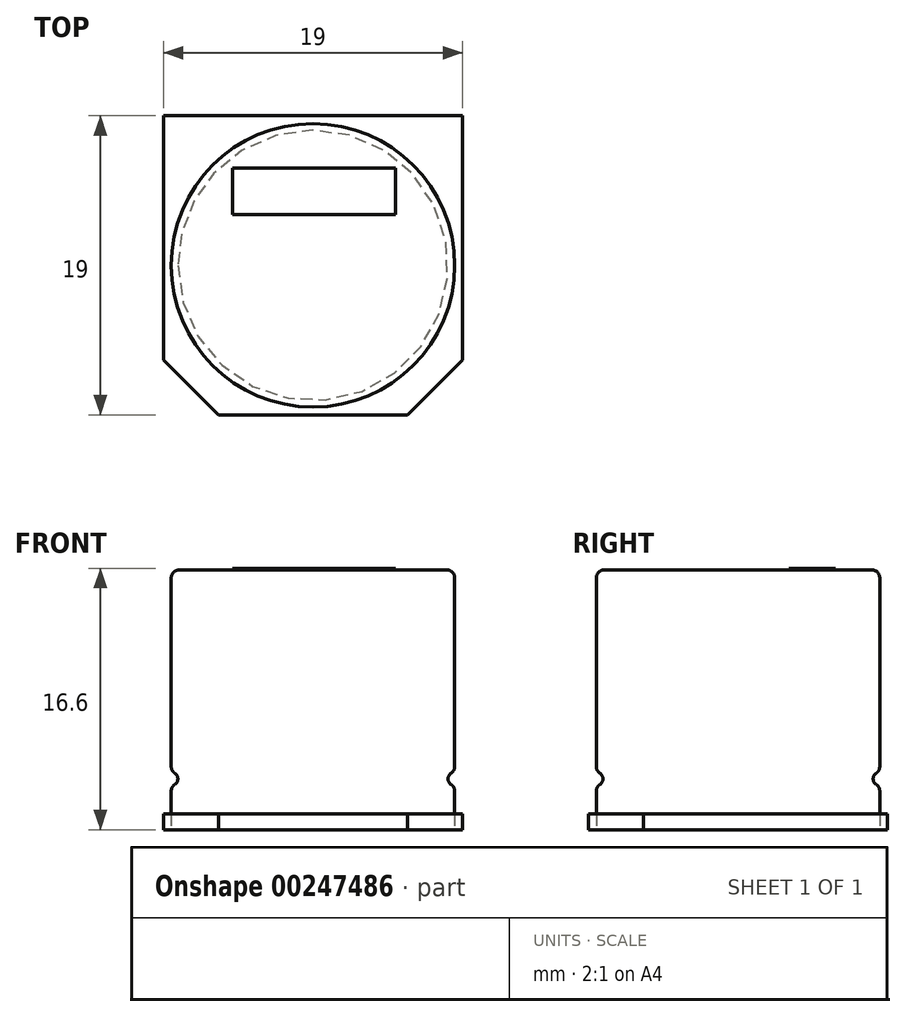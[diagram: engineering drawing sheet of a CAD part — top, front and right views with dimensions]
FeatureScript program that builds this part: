
annotation { "Feature Type Name" : "Feature", "Feature Type Description" : "" }
export const myFeature = defineFeature(function(context is Context, id is Id, definition is map)
    precondition{}
    {
        {
            var Q0;
            Q0=qCreatedBy(makeId("Front.planeOp"),FACE);
            var sketch = newSketch(context, id + "F0", { "sketchPlane" : qUnion([Q0])});
            skLineSegment(sketch, "E0.bottom", {"start": v(0, 0) * mm, "end": v(9, 0) * mm});
            skLineSegment(sketch, "E0.top", {"start": v(0, 16.5) * mm, "end": v(9, 16.5) * mm});
            skLineSegment(sketch, "E0.left", {"start": v(0, 0) * mm, "end": v(0, 16.5) * mm});
            skLineSegment(sketch, "E0.right", {"start": v(9, 0) * mm, "end": v(9, 2.8) * mm});
            skArc(sketch, "E1", {"start": v(9, 3.66) * mm, "mid": v(8.58, 3.23) * mm, "end": v(9, 2.8) * mm});
            skLineSegment(sketch, "E2.trimOffspring", {"start": v(9, 3.66) * mm, "end": v(9, 16.5) * mm});
            skSolve(sketch);
        }
        {
            var Q0;
            Q0=makeQuery(id+"F0.imprint","IMPRINT",FACE,{"disambiguationData":[TD([[makeQuery(id+"F0.imprint","IMPRINT",EDGE,{"derivedFrom":sQuery(id+"F0.wireOp",EDGE,"E0.bottom")}),1.0]])]});
            var Q1;
            Q1=sQuery(id+"F0.wireOp",EDGE,"E0.left");
            revolve(context, id + "F1", {"entities" : qUnion([Q0]), "axis" : qUnion([Q1]), "revolveType" : RevolveType.FULL});
        }
        {
            var Q0;
            Q0=makeQuery(id+"F1.opRevolve","SWEPT_EDGE",EDGE,{"disambiguationData":[OSD([sQuery(id+"F0.wireOp",EDGE,"E0.top"),sQuery(id+"F0.wireOp",EDGE,"E2.trimOffspring")])]});
            var Q1;
            Q1=makeQuery(id+"F1.opRevolve","SWEPT_EDGE",EDGE,{"disambiguationData":[OSD([sQuery(id+"F0.wireOp",EDGE,"E1"),sQuery(id+"F0.wireOp",EDGE,"E2.trimOffspring")])]});
            var Q2;
            Q2=makeQuery(id+"F1.opRevolve","SWEPT_EDGE",EDGE,{"disambiguationData":[OSD([sQuery(id+"F0.wireOp",EDGE,"E0.right"),sQuery(id+"F0.wireOp",EDGE,"E1")])]});
            fillet(context, id + "F2", {"entities" : qUnion([Q0, Q1, Q2]), "radius" : .5 * mm, "tangentPropagation" : true, "allowEdgeOverflow" : false});
        }
        {
            var Q0;
            Q0=makeQuery(id+"F1.opRevolve","SWEPT_FACE",FACE,{"disambiguationData":[OSD([sQuery(id+"F0.wireOp",EDGE,"E0.bottom")])]});
            var sketch = newSketch(context, id + "F3", { "sketchPlane" : qUnion([Q0])});
            skLineSegment(sketch, "E3.rect.bottom", {"start": v(9.5, -9.5) * mm, "end": v(-9.5, -9.5) * mm});
            skLineSegment(sketch, "E3.rect.top", {"start": v(9.5, 9.5) * mm, "end": v(-9.5, 9.5) * mm});
            skLineSegment(sketch, "E3.rect.left", {"start": v(9.5, -9.5) * mm, "end": v(9.5, 9.5) * mm});
            skLineSegment(sketch, "E3.rect.right", {"start": v(-9.5, -9.5) * mm, "end": v(-9.5, 9.5) * mm});
            skPoint(sketch, "E3.rect.middle", {"position": v(0, 0) * mm});
            skSolve(sketch);
        }
        {
            var Q0;
            Q0=qSketchRegion(id+"F3",true);
            extrude(context, id + "F4", {"entities" : qUnion([Q0]), "oppositeDirection" : true, "depth" : 1 * mm});
        }
        {
            var Q0;
            Q0=makeQuery(id+"F4.opExtrude","SWEPT_EDGE",EDGE,{"disambiguationData":[OSD([sQuery(id+"F3.wireOp",EDGE,"E3.rect.top"),sQuery(id+"F3.wireOp",EDGE,"E3.rect.right")])]});
            var Q1;
            Q1=makeQuery(id+"F4.opExtrude","SWEPT_EDGE",EDGE,{"disambiguationData":[OSD([sQuery(id+"F3.wireOp",EDGE,"E3.rect.top"),sQuery(id+"F3.wireOp",EDGE,"E3.rect.left")])]});
            chamfer(context, id + "F5", {"entities" : qUnion([Q0, Q1]), "width" : 3.5 * mm, "tangentPropagation" : true});
        }
        {
            var Q0;
            Q0=makeQuery(id+"F1.opRevolve","SWEPT_FACE",FACE,{"disambiguationData":[OSD([sQuery(id+"F0.wireOp",EDGE,"E0.top")])]});
            var sketch = newSketch(context, id + "F6", { "sketchPlane" : qUnion([Q0])});
            skLineSegment(sketch, "E4.bottom", {"start": v(-5.12, 6.19) * mm, "end": v(5.24, 6.19) * mm});
            skLineSegment(sketch, "E4.top", {"start": v(-5.12, 3.24) * mm, "end": v(5.24, 3.24) * mm});
            skLineSegment(sketch, "E4.left", {"start": v(-5.12, 6.19) * mm, "end": v(-5.12, 3.24) * mm});
            skLineSegment(sketch, "E4.right", {"start": v(5.24, 6.19) * mm, "end": v(5.24, 3.24) * mm});
            skSolve(sketch);
        }
        {
            var Q0;
            Q0=makeQuery(id+"F6.imprint","IMPRINT",FACE,{"disambiguationData":[TD([[makeQuery(id+"F6.imprint","IMPRINT",EDGE,{"derivedFrom":sQuery(id+"F6.wireOp",EDGE,"E4.bottom")}),-1.0]])]});
            extrude(context, id + "F7", {"entities" : qUnion([Q0]), "depth" : .1 * mm});
        }
    });
